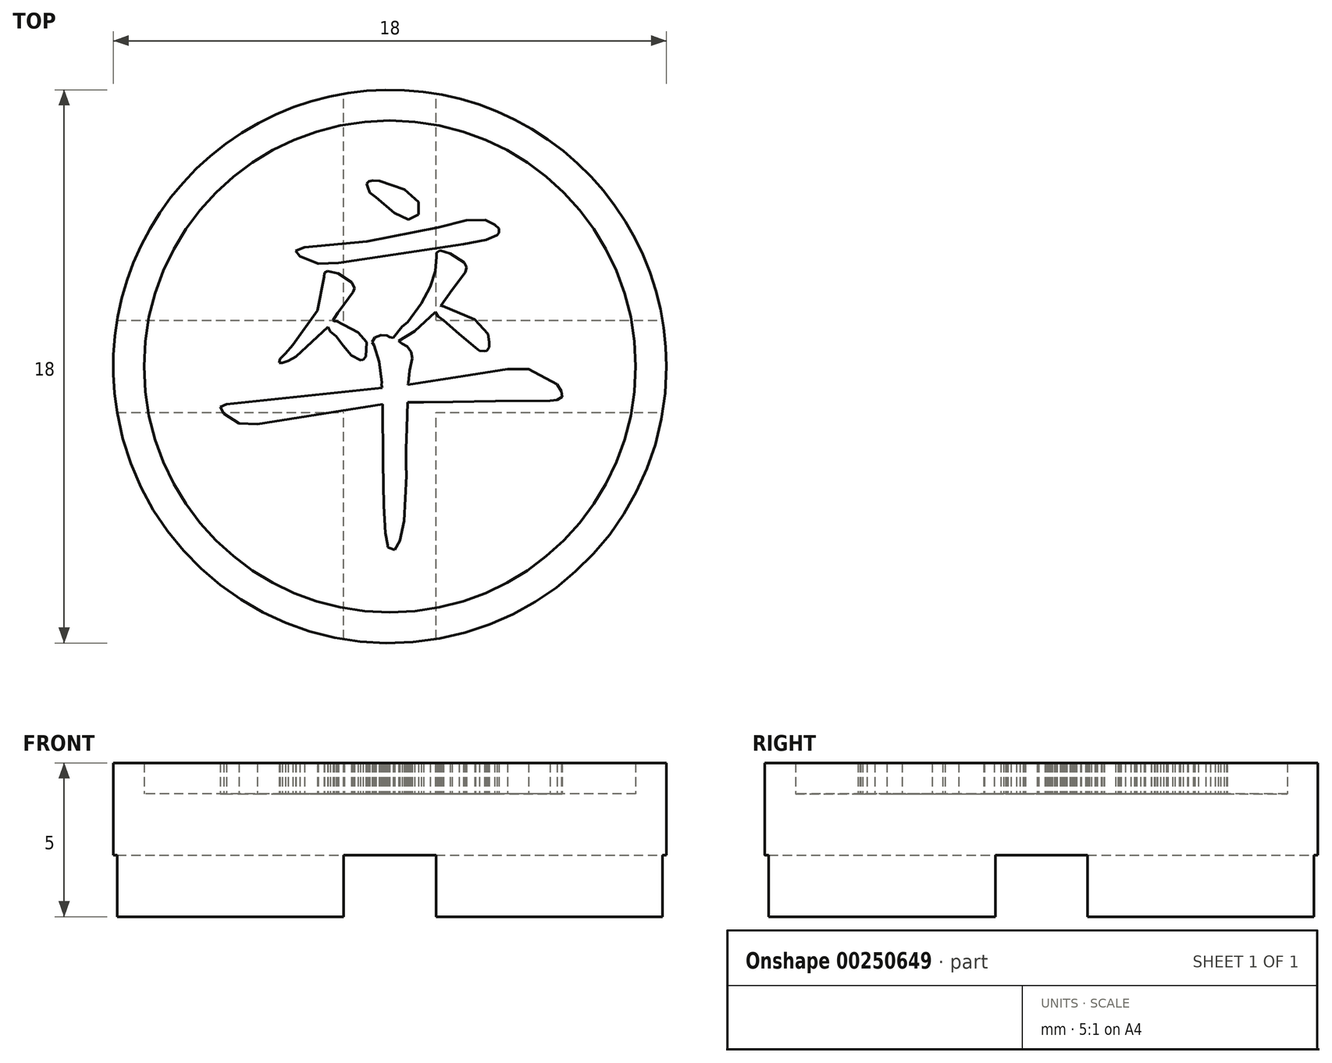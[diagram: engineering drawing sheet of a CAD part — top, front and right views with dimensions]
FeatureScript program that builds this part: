
annotation { "Feature Type Name" : "Feature", "Feature Type Description" : "" }
export const myFeature = defineFeature(function(context is Context, id is Id, definition is map)
    precondition{}
    {
        {
            var Q0;
            Q0=qCreatedBy(makeId("Top.planeOp"),FACE);
            var sketch = newSketch(context, id + "F0", { "sketchPlane" : qUnion([Q0])});
            skCircle(sketch, "E0", {"center": v(-31.33, 19.76) * mm, "radius": 9 * mm});
            skSolve(sketch);
        }
        {
            var Q0;
            Q0=qSketchRegion(id+"F0",true);
            extrude(context, id + "F1", {"entities" : qUnion([Q0]), "depth" : 4 * mm});
        }
        {
            var Q0;
            Q0=makeQuery(id+"F1.opExtrude","CAP_FACE",FACE,{"disambiguationData":[OSD([sQuery(id+"F0.wireOp",EDGE,"E0")])],"isStart":false});
            var sketch = newSketch(context, id + "F2", { "sketchPlane" : qUnion([Q0])});
            skCircle(sketch, "E1", {"center": v(-31.33, 19.76) * mm, "radius": 8 * mm});
            skCircle(sketch, "E2", {"center": v(-31.33, 19.76) * mm, "radius": 9 * mm});
            skSolve(sketch);
        }
        {
            var Q0;
            Q0=makeQuery(id+"F1.opExtrude","CAP_FACE",FACE,{"disambiguationData":[OSD([sQuery(id+"F0.wireOp",EDGE,"E0")])],"isStart":true});
            var sketch = newSketch(context, id + "F3", { "sketchPlane" : qUnion([Q0])});
            skLineSegment(sketch, "E3", {"start": v(-31.33, -19.76) * mm, "end": v(-22.33, -19.76) * mm, "construction": true});
            skLineSegment(sketch, "E4", {"start": v(-31.33, -19.76) * mm, "end": v(-31.33, -10.76) * mm, "construction": true});
            skLineSegment(sketch, "E5", {"start": v(-31.33, -19.76) * mm, "end": v(-40.33, -19.76) * mm, "construction": true});
            skLineSegment(sketch, "E6", {"start": v(-31.33, -19.76) * mm, "end": v(-31.33, -28.76) * mm, "construction": true});
            skLineSegment(sketch, "E7.bottom", {"start": v(-40.33, -28.76) * mm, "end": v(-22.33, -28.76) * mm});
            skLineSegment(sketch, "E7.top", {"start": v(-40.33, -10.76) * mm, "end": v(-22.33, -10.76) * mm});
            skLineSegment(sketch, "E7.left", {"start": v(-22.33, -10.76) * mm, "end": v(-22.33, -28.76) * mm});
            skLineSegment(sketch, "E7.right", {"start": v(-40.33, -10.76) * mm, "end": v(-40.33, -28.76) * mm});
            skPoint(sketch, "E8", {"position": v(-31.33, -28.76) * mm});
            skPoint(sketch, "E9", {"position": v(-40.33, -19.76) * mm});
            skPoint(sketch, "E10", {"position": v(-22.33, -19.76) * mm});
            skPoint(sketch, "E11", {"position": v(-31.33, -10.76) * mm});
            skLineSegment(sketch, "E12.bottom", {"start": v(-32.83, -10.76) * mm, "end": v(-29.83, -10.76) * mm});
            skLineSegment(sketch, "E12.top", {"start": v(-32.83, -28.76) * mm, "end": v(-29.83, -28.76) * mm});
            skLineSegment(sketch, "E12.left", {"start": v(-32.83, -10.76) * mm, "end": v(-32.83, -28.76) * mm});
            skLineSegment(sketch, "E12.right", {"start": v(-29.83, -10.76) * mm, "end": v(-29.83, -28.76) * mm});
            skLineSegment(sketch, "E13.bottom", {"start": v(-40.33, -18.26) * mm, "end": v(-22.33, -18.26) * mm});
            skLineSegment(sketch, "E13.top", {"start": v(-40.33, -21.26) * mm, "end": v(-22.33, -21.26) * mm});
            skLineSegment(sketch, "E13.left", {"start": v(-40.33, -18.26) * mm, "end": v(-40.33, -21.26) * mm});
            skLineSegment(sketch, "E13.right", {"start": v(-22.33, -18.26) * mm, "end": v(-22.33, -21.26) * mm});
            skSolve(sketch);
        }
        {
            var Q0;
            {var subQ1=sQuery(id+"F3.wireOp",EDGE,"E12.bottom");var subQ3=makeQuery(id+"F1.opExtrude","CAP_EDGE",EDGE,{"disambiguationData":[OSD([sQuery(id+"F0.wireOp",EDGE,"E0")])],"isStart":true});var subQ4=makeQuery(id+"F3.imprint","INTERSECT",VERTEX,{"derivedFrom":[subQ3,subQ1]});Q0=makeQuery(id+"F3.imprint","IMPRINT",FACE,{"disambiguationData":[TD([[makeQuery(id+"F3.imprint","IMPRINT",EDGE,{"disambiguationData":[TD([[subQ4,1.0]])],"derivedFrom":subQ3}),1.0]])]});}
            var Q1;
            {var subQ1=sQuery(id+"F3.wireOp",EDGE,"E12.bottom");var subQ3=makeQuery(id+"F1.opExtrude","CAP_EDGE",EDGE,{"disambiguationData":[OSD([sQuery(id+"F0.wireOp",EDGE,"E0")])],"isStart":true});var subQ4=makeQuery(id+"F3.imprint","INTERSECT",VERTEX,{"derivedFrom":[subQ3,subQ1]});Q1=makeQuery(id+"F3.imprint","IMPRINT",FACE,{"disambiguationData":[TD([[makeQuery(id+"F3.imprint","IMPRINT",EDGE,{"disambiguationData":[TD([[subQ4,-1.0]])],"derivedFrom":subQ3}),1.0]])]});}
            var Q2;
            {var subQ1=sQuery(id+"F3.wireOp",EDGE,"E12.top");var subQ3=makeQuery(id+"F1.opExtrude","CAP_EDGE",EDGE,{"disambiguationData":[OSD([sQuery(id+"F0.wireOp",EDGE,"E0")])],"isStart":true});var subQ4=makeQuery(id+"F3.imprint","INTERSECT",VERTEX,{"derivedFrom":[subQ3,subQ1]});Q2=makeQuery(id+"F3.imprint","IMPRINT",FACE,{"disambiguationData":[TD([[makeQuery(id+"F3.imprint","IMPRINT",EDGE,{"disambiguationData":[TD([[subQ4,-1.0]])],"derivedFrom":subQ3}),1.0]])]});}
            var Q3;
            {var subQ1=sQuery(id+"F3.wireOp",EDGE,"E12.top");var subQ3=makeQuery(id+"F1.opExtrude","CAP_EDGE",EDGE,{"disambiguationData":[OSD([sQuery(id+"F0.wireOp",EDGE,"E0")])],"isStart":true});var subQ4=makeQuery(id+"F3.imprint","INTERSECT",VERTEX,{"derivedFrom":[subQ3,subQ1]});Q3=makeQuery(id+"F3.imprint","IMPRINT",FACE,{"disambiguationData":[TD([[makeQuery(id+"F3.imprint","IMPRINT",EDGE,{"disambiguationData":[TD([[subQ4,1.0]])],"derivedFrom":subQ3}),1.0]])]});}
            var Q4;
            {var subQ0=sQuery(id+"F3.wireOp",EDGE,"E13.left");var subQ3=makeQuery(id+"F1.opExtrude","CAP_EDGE",EDGE,{"disambiguationData":[OSD([sQuery(id+"F0.wireOp",EDGE,"E0")])],"isStart":true});var subQ5=makeQuery(id+"F3.imprint","INTERSECT",VERTEX,{"derivedFrom":[subQ3,subQ0]});Q4=makeQuery(id+"F3.imprint","IMPRINT",FACE,{"disambiguationData":[TD([[makeQuery(id+"F3.imprint","IMPRINT",EDGE,{"disambiguationData":[TD([[subQ5,-1.0]])],"derivedFrom":subQ3}),1.0]])]});}
            var Q5;
            {var subQ0=sQuery(id+"F3.wireOp",EDGE,"E13.right");var subQ3=makeQuery(id+"F1.opExtrude","CAP_EDGE",EDGE,{"disambiguationData":[OSD([sQuery(id+"F0.wireOp",EDGE,"E0")])],"isStart":true});var subQ5=makeQuery(id+"F3.imprint","INTERSECT",VERTEX,{"derivedFrom":[subQ3,subQ0]});Q5=makeQuery(id+"F3.imprint","IMPRINT",FACE,{"disambiguationData":[TD([[makeQuery(id+"F3.imprint","IMPRINT",EDGE,{"disambiguationData":[TD([[subQ5,1.0]])],"derivedFrom":subQ3}),1.0]])]});}
            var Q6;
            {var subQ0=sQuery(id+"F3.wireOp",EDGE,"E13.left");var subQ3=makeQuery(id+"F1.opExtrude","CAP_EDGE",EDGE,{"disambiguationData":[OSD([sQuery(id+"F0.wireOp",EDGE,"E0")])],"isStart":true});var subQ5=makeQuery(id+"F3.imprint","INTERSECT",VERTEX,{"derivedFrom":[subQ3,subQ0]});Q6=makeQuery(id+"F3.imprint","IMPRINT",FACE,{"disambiguationData":[TD([[makeQuery(id+"F3.imprint","IMPRINT",EDGE,{"disambiguationData":[TD([[subQ5,1.0]])],"derivedFrom":subQ3}),1.0]])]});}
            var Q7;
            {var subQ0=sQuery(id+"F3.wireOp",EDGE,"E13.right");var subQ3=makeQuery(id+"F1.opExtrude","CAP_EDGE",EDGE,{"disambiguationData":[OSD([sQuery(id+"F0.wireOp",EDGE,"E0")])],"isStart":true});var subQ5=makeQuery(id+"F3.imprint","INTERSECT",VERTEX,{"derivedFrom":[subQ3,subQ0]});Q7=makeQuery(id+"F3.imprint","IMPRINT",FACE,{"disambiguationData":[TD([[makeQuery(id+"F3.imprint","IMPRINT",EDGE,{"disambiguationData":[TD([[subQ5,-1.0]])],"derivedFrom":subQ3}),1.0]])]});}
            var Q8;
            {var subQ3=makeQuery(id+"F1.opExtrude","CAP_EDGE",EDGE,{"disambiguationData":[OSD([sQuery(id+"F0.wireOp",EDGE,"E0")])],"isStart":true});var subQ5=sQuery(id+"F3.wireOp",EDGE,"E12.left");var subQ8=makeQuery(id+"F3.imprint","INTERSECT",VERTEX,{"disambiguationData":[OD(1.0)],"derivedFrom":[subQ3,subQ5]});Q8=makeQuery(id+"F3.imprint","IMPRINT",FACE,{"disambiguationData":[TD([[makeQuery(id+"F3.imprint","IMPRINT",EDGE,{"disambiguationData":[TD([[subQ8,-1.0]])],"derivedFrom":subQ3}),1.0]])]});}
            var Q9;
            {var subQ3=makeQuery(id+"F1.opExtrude","CAP_EDGE",EDGE,{"disambiguationData":[OSD([sQuery(id+"F0.wireOp",EDGE,"E0")])],"isStart":true});var subQ5=sQuery(id+"F3.wireOp",EDGE,"E12.right");var subQ8=makeQuery(id+"F3.imprint","INTERSECT",VERTEX,{"disambiguationData":[OD(1.0)],"derivedFrom":[subQ3,subQ5]});Q9=makeQuery(id+"F3.imprint","IMPRINT",FACE,{"disambiguationData":[TD([[makeQuery(id+"F3.imprint","IMPRINT",EDGE,{"disambiguationData":[TD([[subQ8,1.0]])],"derivedFrom":subQ3}),1.0]])]});}
            var Q10;
            {var subQ3=makeQuery(id+"F1.opExtrude","CAP_EDGE",EDGE,{"disambiguationData":[OSD([sQuery(id+"F0.wireOp",EDGE,"E0")])],"isStart":true});var subQ5=sQuery(id+"F3.wireOp",EDGE,"E12.left");var subQ8=makeQuery(id+"F3.imprint","INTERSECT",VERTEX,{"disambiguationData":[OD(0.0)],"derivedFrom":[subQ3,subQ5]});Q10=makeQuery(id+"F3.imprint","IMPRINT",FACE,{"disambiguationData":[TD([[makeQuery(id+"F3.imprint","IMPRINT",EDGE,{"disambiguationData":[TD([[subQ8,1.0]])],"derivedFrom":subQ3}),1.0]])]});}
            var Q11;
            {var subQ3=makeQuery(id+"F1.opExtrude","CAP_EDGE",EDGE,{"disambiguationData":[OSD([sQuery(id+"F0.wireOp",EDGE,"E0")])],"isStart":true});var subQ5=sQuery(id+"F3.wireOp",EDGE,"E12.right");var subQ8=makeQuery(id+"F3.imprint","INTERSECT",VERTEX,{"disambiguationData":[OD(0.0)],"derivedFrom":[subQ3,subQ5]});Q11=makeQuery(id+"F3.imprint","IMPRINT",FACE,{"disambiguationData":[TD([[makeQuery(id+"F3.imprint","IMPRINT",EDGE,{"disambiguationData":[TD([[subQ8,-1.0]])],"derivedFrom":subQ3}),1.0]])]});}
            var Q12;
            {var subQ2=sQuery(id+"F3.wireOp",EDGE,"E12.left");var subQ4=sQuery(id+"F3.wireOp",EDGE,"E13.bottom");var subQ8=makeQuery(id+"F3.imprint","INTERSECT",VERTEX,{"derivedFrom":[subQ2,subQ4]});Q12=makeQuery(id+"F3.imprint","IMPRINT",FACE,{"disambiguationData":[TD([[makeQuery(id+"F3.imprint","IMPRINT",EDGE,{"disambiguationData":[TD([[subQ8,1.0]])],"derivedFrom":subQ2}),1.0]])]});}
            var Q13;
            {var subQ1=sQuery(id+"F3.wireOp",EDGE,"E12.left");var subQ5=sQuery(id+"F3.wireOp",EDGE,"E13.bottom");var subQ6=makeQuery(id+"F3.imprint","INTERSECT",VERTEX,{"derivedFrom":[subQ1,subQ5]});Q13=makeQuery(id+"F3.imprint","IMPRINT",FACE,{"disambiguationData":[TD([[makeQuery(id+"F3.imprint","IMPRINT",EDGE,{"disambiguationData":[TD([[subQ6,-1.0]])],"derivedFrom":subQ1}),-1.0]])]});}
            var Q14;
            {var subQ0=sQuery(id+"F3.wireOp",EDGE,"E13.top");var subQ1=sQuery(id+"F3.wireOp",EDGE,"E12.left");var subQ2=makeQuery(id+"F3.imprint","INTERSECT",VERTEX,{"derivedFrom":[subQ1,subQ0]});Q14=makeQuery(id+"F3.imprint","IMPRINT",FACE,{"disambiguationData":[TD([[makeQuery(id+"F3.imprint","IMPRINT",EDGE,{"disambiguationData":[TD([[subQ2,-1.0]])],"derivedFrom":subQ1}),1.0]])]});}
            var Q15;
            {var subQ2=sQuery(id+"F3.wireOp",EDGE,"E13.bottom");var subQ5=sQuery(id+"F3.wireOp",EDGE,"E12.right");var subQ8=makeQuery(id+"F3.imprint","INTERSECT",VERTEX,{"derivedFrom":[subQ5,subQ2]});Q15=makeQuery(id+"F3.imprint","IMPRINT",FACE,{"disambiguationData":[TD([[makeQuery(id+"F3.imprint","IMPRINT",EDGE,{"disambiguationData":[TD([[subQ8,-1.0]])],"derivedFrom":subQ5}),1.0]])]});}
            var Q16;
            {var subQ0=sQuery(id+"F3.wireOp",EDGE,"E13.bottom");var subQ1=sQuery(id+"F3.wireOp",EDGE,"E12.left");var subQ2=makeQuery(id+"F3.imprint","INTERSECT",VERTEX,{"derivedFrom":[subQ1,subQ0]});Q16=makeQuery(id+"F3.imprint","IMPRINT",FACE,{"disambiguationData":[TD([[makeQuery(id+"F3.imprint","IMPRINT",EDGE,{"disambiguationData":[TD([[subQ2,-1.0]])],"derivedFrom":subQ1}),1.0]])]});}
            extrude(context, id + "F4", {"entities" : qUnion([Q0, Q1, Q2, Q3, Q4, Q5, Q6, Q7, Q8, Q9, Q10, Q11, Q12, Q13, Q14, Q15, Q16]), "operationType" : NewBodyOperationType.REMOVE, "oppositeDirection" : true, "depth" : 2 * mm});
        }
        {
            var Q0;
            Q0=qSketchRegion(id+"F2",true);
            var Q1;
            Q1=makeQuery(id+"F2.imprint","IMPRINT",FACE,{"disambiguationData":[TD([[makeQuery(id+"F2.imprint","IMPRINT",EDGE,{"derivedFrom":sQuery(id+"F2.wireOp",EDGE,"hKqnuJLd-dfdz-vJIs-yDKo-c4hLNRw30SuP")}),-1.0]])]});
            extrude(context, id + "F5", {"entities" : qUnion([Q0, Q1]), "operationType" : NewBodyOperationType.ADD, "depth" : 1 * mm});
        }
        {
            var Q0;
            Q0=makeQuery(id+"F1.opExtrude","CAP_FACE",FACE,{"disambiguationData":[OSD([sQuery(id+"F0.wireOp",EDGE,"E0")])],"isStart":false});
            var sketch = newSketch(context, id + "F6", { "sketchPlane" : qUnion([Q0])});
            skLineSegment(sketch, "E14", {"start": v(-31.78, 25.26) * mm, "end": v(-31.19, 24.76) * mm});
            skLineSegment(sketch, "E15", {"start": v(-31.19, 24.76) * mm, "end": v(-30.72, 24.53) * mm});
            skLineSegment(sketch, "E16", {"start": v(-30.72, 24.53) * mm, "end": v(-30.4, 24.7) * mm});
            skLineSegment(sketch, "E17", {"start": v(-30.4, 24.7) * mm, "end": v(-30.4, 24.87) * mm});
            skLineSegment(sketch, "E18", {"start": v(-30.4, 24.87) * mm, "end": v(-30.4, 25.1) * mm});
            skLineSegment(sketch, "E19", {"start": v(-30.4, 25.1) * mm, "end": v(-30.85, 25.52) * mm});
            skLineSegment(sketch, "E20", {"start": v(-30.85, 25.52) * mm, "end": v(-31.66, 25.8) * mm});
            skLineSegment(sketch, "E21", {"start": v(-31.66, 25.8) * mm, "end": v(-31.88, 25.8) * mm});
            skLineSegment(sketch, "E22", {"start": v(-31.88, 25.8) * mm, "end": v(-32, 25.78) * mm});
            skLineSegment(sketch, "E23", {"start": v(-32, 25.78) * mm, "end": v(-32.09, 25.7) * mm});
            skLineSegment(sketch, "E24", {"start": v(-32.09, 25.7) * mm, "end": v(-32.04, 25.59) * mm});
            skLineSegment(sketch, "E25", {"start": v(-32.04, 25.59) * mm, "end": v(-31.98, 25.42) * mm});
            skLineSegment(sketch, "E26", {"start": v(-31.98, 25.42) * mm, "end": v(-31.78, 25.26) * mm});
            skLineSegment(sketch, "E27", {"start": v(-34.1, 23.64) * mm, "end": v(-34.4, 23.52) * mm});
            skLineSegment(sketch, "E28", {"start": v(-34.4, 23.52) * mm, "end": v(-34.25, 23.35) * mm});
            skLineSegment(sketch, "E29", {"start": v(-34.25, 23.35) * mm, "end": v(-33.66, 23.1) * mm});
            skLineSegment(sketch, "E30", {"start": v(-33.66, 23.1) * mm, "end": v(-33, 23.13) * mm});
            skLineSegment(sketch, "E31", {"start": v(-33, 23.13) * mm, "end": v(-28.93, 23.73) * mm});
            skLineSegment(sketch, "E32", {"start": v(-28.93, 23.73) * mm, "end": v(-28.2, 23.88) * mm});
            skLineSegment(sketch, "E33", {"start": v(-28.2, 23.88) * mm, "end": v(-27.84, 24.03) * mm});
            skLineSegment(sketch, "E34", {"start": v(-27.84, 24.03) * mm, "end": v(-27.78, 24.1) * mm});
            skLineSegment(sketch, "E35", {"start": v(-27.78, 24.1) * mm, "end": v(-27.77, 24.24) * mm});
            skLineSegment(sketch, "E36", {"start": v(-27.77, 24.24) * mm, "end": v(-27.93, 24.37) * mm});
            skLineSegment(sketch, "E37", {"start": v(-27.93, 24.37) * mm, "end": v(-28.22, 24.52) * mm});
            skLineSegment(sketch, "E38", {"start": v(-28.22, 24.52) * mm, "end": v(-28.84, 24.51) * mm});
            skLineSegment(sketch, "E39", {"start": v(-28.84, 24.51) * mm, "end": v(-29.75, 24.28) * mm});
            skLineSegment(sketch, "E40", {"start": v(-29.75, 24.28) * mm, "end": v(-32.07, 23.82) * mm});
            skLineSegment(sketch, "E41", {"start": v(-32.07, 23.82) * mm, "end": v(-34.1, 23.64) * mm});
            skLineSegment(sketch, "E42", {"start": v(-33.34, 21.04) * mm, "end": v(-33.26, 20.9) * mm});
            skLineSegment(sketch, "E43", {"start": v(-33.26, 20.9) * mm, "end": v(-33.07, 20.73) * mm});
            skLineSegment(sketch, "E44", {"start": v(-33.07, 20.73) * mm, "end": v(-32.85, 20.44) * mm});
            skLineSegment(sketch, "E45", {"start": v(-32.85, 20.44) * mm, "end": v(-32.58, 20.12) * mm});
            skLineSegment(sketch, "E46", {"start": v(-32.58, 20.12) * mm, "end": v(-32.29, 19.96) * mm});
            skLineSegment(sketch, "E47", {"start": v(-32.29, 19.96) * mm, "end": v(-32.2, 19.98) * mm});
            skLineSegment(sketch, "E48", {"start": v(-32.2, 19.98) * mm, "end": v(-32.1, 20.08) * mm});
            skLineSegment(sketch, "E49", {"start": v(-32.1, 20.08) * mm, "end": v(-32.08, 20.54) * mm});
            skLineSegment(sketch, "E50", {"start": v(-32.08, 20.54) * mm, "end": v(-32.37, 20.87) * mm});
            skLineSegment(sketch, "E51", {"start": v(-32.37, 20.87) * mm, "end": v(-33.06, 21.23) * mm});
            skLineSegment(sketch, "E52", {"start": v(-33.06, 21.23) * mm, "end": v(-33.15, 21.23) * mm});
            skLineSegment(sketch, "E53", {"start": v(-33.15, 21.23) * mm, "end": v(-33.18, 21.26) * mm});
            skLineSegment(sketch, "E54", {"start": v(-33.18, 21.26) * mm, "end": v(-33.15, 21.32) * mm});
            skLineSegment(sketch, "E55", {"start": v(-33.15, 21.32) * mm, "end": v(-33.02, 21.5) * mm});
            skLineSegment(sketch, "E56", {"start": v(-33.02, 21.5) * mm, "end": v(-32.81, 21.8) * mm});
            skLineSegment(sketch, "E57", {"start": v(-32.81, 21.8) * mm, "end": v(-32.53, 22.17) * mm});
            skLineSegment(sketch, "E58", {"start": v(-32.53, 22.17) * mm, "end": v(-32.49, 22.3) * mm});
            skLineSegment(sketch, "E59", {"start": v(-32.49, 22.3) * mm, "end": v(-32.56, 22.49) * mm});
            skLineSegment(sketch, "E60", {"start": v(-32.56, 22.49) * mm, "end": v(-33.02, 22.78) * mm});
            skLineSegment(sketch, "E61", {"start": v(-33.02, 22.78) * mm, "end": v(-33.35, 22.87) * mm});
            skLineSegment(sketch, "E62", {"start": v(-33.35, 22.87) * mm, "end": v(-33.46, 22.8) * mm});
            skLineSegment(sketch, "E63", {"start": v(-33.46, 22.8) * mm, "end": v(-33.47, 22.68) * mm});
            skLineSegment(sketch, "E64", {"start": v(-33.47, 22.68) * mm, "end": v(-33.69, 21.58) * mm});
            skLineSegment(sketch, "E65", {"start": v(-33.69, 21.58) * mm, "end": v(-34.48, 20.46) * mm});
            skLineSegment(sketch, "E66", {"start": v(-34.48, 20.46) * mm, "end": v(-34.73, 20.18) * mm});
            skLineSegment(sketch, "E67", {"start": v(-34.73, 20.18) * mm, "end": v(-34.9, 20) * mm});
            skLineSegment(sketch, "E68", {"start": v(-34.9, 20) * mm, "end": v(-34.93, 19.88) * mm});
            skLineSegment(sketch, "E69", {"start": v(-34.93, 19.88) * mm, "end": v(-34.83, 19.88) * mm});
            skLineSegment(sketch, "E70", {"start": v(-34.83, 19.88) * mm, "end": v(-34.64, 19.94) * mm});
            skLineSegment(sketch, "E71", {"start": v(-34.64, 19.94) * mm, "end": v(-34.38, 20.08) * mm});
            skLineSegment(sketch, "E72", {"start": v(-34.38, 20.08) * mm, "end": v(-33.34, 21.04) * mm});
            skLineSegment(sketch, "E73", {"start": v(-31.56, 18.54) * mm, "end": v(-31.55, 16.62) * mm});
            skLineSegment(sketch, "E74", {"start": v(-31.55, 16.62) * mm, "end": v(-31.52, 15.23) * mm});
            skLineSegment(sketch, "E75", {"start": v(-31.52, 15.23) * mm, "end": v(-31.47, 14.34) * mm});
            skLineSegment(sketch, "E76", {"start": v(-31.47, 14.34) * mm, "end": v(-31.4, 13.94) * mm});
            skLineSegment(sketch, "E77", {"start": v(-31.4, 13.94) * mm, "end": v(-31.4, 13.88) * mm});
            skLineSegment(sketch, "E78", {"start": v(-31.4, 13.88) * mm, "end": v(-31.34, 13.86) * mm});
            skLineSegment(sketch, "E79", {"start": v(-31.34, 13.86) * mm, "end": v(-31.17, 13.8) * mm});
            skLineSegment(sketch, "E80", {"start": v(-31.17, 13.8) * mm, "end": v(-31, 14.08) * mm});
            skLineSegment(sketch, "E81", {"start": v(-31, 14.08) * mm, "end": v(-30.86, 14.73) * mm});
            skLineSegment(sketch, "E82", {"start": v(-30.86, 14.73) * mm, "end": v(-30.79, 16.2) * mm});
            skLineSegment(sketch, "E83", {"start": v(-30.79, 16.2) * mm, "end": v(-30.8, 16.55) * mm});
            skLineSegment(sketch, "E84", {"start": v(-30.8, 16.55) * mm, "end": v(-30.8, 17.06) * mm});
            skLineSegment(sketch, "E85", {"start": v(-30.8, 17.06) * mm, "end": v(-30.78, 17.75) * mm});
            skLineSegment(sketch, "E86", {"start": v(-30.78, 17.75) * mm, "end": v(-30.75, 18.6) * mm});
            skLineSegment(sketch, "E87", {"start": v(-30.75, 18.6) * mm, "end": v(-30.23, 18.59) * mm});
            skLineSegment(sketch, "E88", {"start": v(-30.23, 18.59) * mm, "end": v(-29.27, 18.6) * mm});
            skLineSegment(sketch, "E89", {"start": v(-29.27, 18.6) * mm, "end": v(-27.9, 18.63) * mm});
            skLineSegment(sketch, "E90", {"start": v(-27.9, 18.63) * mm, "end": v(-26.12, 18.65) * mm});
            skLineSegment(sketch, "E91", {"start": v(-26.12, 18.65) * mm, "end": v(-25.89, 18.67) * mm});
            skLineSegment(sketch, "E92", {"start": v(-25.89, 18.67) * mm, "end": v(-25.73, 18.77) * mm});
            skLineSegment(sketch, "E93", {"start": v(-25.73, 18.77) * mm, "end": v(-25.75, 18.95) * mm});
            skLineSegment(sketch, "E94", {"start": v(-25.75, 18.95) * mm, "end": v(-25.9, 19.18) * mm});
            skLineSegment(sketch, "E95", {"start": v(-25.9, 19.18) * mm, "end": v(-26.81, 19.67) * mm});
            skLineSegment(sketch, "E96", {"start": v(-26.81, 19.67) * mm, "end": v(-27.5, 19.67) * mm});
            skLineSegment(sketch, "E97", {"start": v(-27.5, 19.67) * mm, "end": v(-28.95, 19.44) * mm});
            skLineSegment(sketch, "E98", {"start": v(-28.95, 19.44) * mm, "end": v(-30.73, 19.17) * mm});
            skLineSegment(sketch, "E99", {"start": v(-30.73, 19.17) * mm, "end": v(-30.76, 19.19) * mm});
            skLineSegment(sketch, "E100", {"start": v(-30.76, 19.19) * mm, "end": v(-30.72, 19.23) * mm});
            skLineSegment(sketch, "E101", {"start": v(-30.72, 19.23) * mm, "end": v(-30.69, 19.62) * mm});
            skLineSegment(sketch, "E102", {"start": v(-30.69, 19.62) * mm, "end": v(-30.6, 20.04) * mm});
            skLineSegment(sketch, "E103", {"start": v(-30.6, 20.04) * mm, "end": v(-30.64, 20.23) * mm});
            skLineSegment(sketch, "E104", {"start": v(-30.64, 20.23) * mm, "end": v(-30.76, 20.42) * mm});
            skLineSegment(sketch, "E105", {"start": v(-30.76, 20.42) * mm, "end": v(-30.93, 20.5) * mm});
            skLineSegment(sketch, "E106", {"start": v(-30.93, 20.5) * mm, "end": v(-31.04, 20.6) * mm});
            skLineSegment(sketch, "E107", {"start": v(-31.04, 20.6) * mm, "end": v(-30.52, 20.91) * mm});
            skLineSegment(sketch, "E108", {"start": v(-30.52, 20.91) * mm, "end": v(-29.85, 21.52) * mm});
            skLineSegment(sketch, "E109", {"start": v(-29.85, 21.52) * mm, "end": v(-29.76, 21.39) * mm});
            skLineSegment(sketch, "E110", {"start": v(-29.76, 21.39) * mm, "end": v(-29.58, 21.26) * mm});
            skLineSegment(sketch, "E111", {"start": v(-29.58, 21.26) * mm, "end": v(-29.08, 20.82) * mm});
            skLineSegment(sketch, "E112", {"start": v(-29.08, 20.82) * mm, "end": v(-28.54, 20.37) * mm});
            skLineSegment(sketch, "E113", {"start": v(-28.54, 20.37) * mm, "end": v(-28.41, 20.26) * mm});
            skLineSegment(sketch, "E114", {"start": v(-28.41, 20.26) * mm, "end": v(-28.25, 20.25) * mm});
            skLineSegment(sketch, "E115", {"start": v(-28.25, 20.25) * mm, "end": v(-28.17, 20.27) * mm});
            skLineSegment(sketch, "E116", {"start": v(-28.17, 20.27) * mm, "end": v(-28.1, 20.39) * mm});
            skLineSegment(sketch, "E117", {"start": v(-28.1, 20.39) * mm, "end": v(-28.1, 20.55) * mm});
            skLineSegment(sketch, "E118", {"start": v(-28.1, 20.55) * mm, "end": v(-28.13, 20.82) * mm});
            skLineSegment(sketch, "E119", {"start": v(-28.13, 20.82) * mm, "end": v(-28.57, 21.28) * mm});
            skLineSegment(sketch, "E120", {"start": v(-28.57, 21.28) * mm, "end": v(-29.62, 21.72) * mm});
            skLineSegment(sketch, "E121", {"start": v(-29.62, 21.72) * mm, "end": v(-29.66, 21.71) * mm});
            skLineSegment(sketch, "E122", {"start": v(-29.66, 21.71) * mm, "end": v(-29.67, 21.72) * mm});
            skLineSegment(sketch, "E123", {"start": v(-29.67, 21.72) * mm, "end": v(-29.3, 22.25) * mm});
            skLineSegment(sketch, "E124", {"start": v(-29.3, 22.25) * mm, "end": v(-28.87, 22.83) * mm});
            skLineSegment(sketch, "E125", {"start": v(-28.87, 22.83) * mm, "end": v(-28.84, 22.98) * mm});
            skLineSegment(sketch, "E126", {"start": v(-28.84, 22.98) * mm, "end": v(-28.9, 23.15) * mm});
            skLineSegment(sketch, "E127", {"start": v(-28.9, 23.15) * mm, "end": v(-29.37, 23.44) * mm});
            skLineSegment(sketch, "E128", {"start": v(-29.37, 23.44) * mm, "end": v(-29.7, 23.53) * mm});
            skLineSegment(sketch, "E129", {"start": v(-29.7, 23.53) * mm, "end": v(-29.81, 23.46) * mm});
            skLineSegment(sketch, "E130", {"start": v(-29.81, 23.46) * mm, "end": v(-29.8, 23.33) * mm});
            skLineSegment(sketch, "E131", {"start": v(-29.8, 23.33) * mm, "end": v(-29.85, 22.86) * mm});
            skLineSegment(sketch, "E132", {"start": v(-29.85, 22.86) * mm, "end": v(-30, 22.36) * mm});
            skLineSegment(sketch, "E133", {"start": v(-30, 22.36) * mm, "end": v(-30.3, 21.8) * mm});
            skLineSegment(sketch, "E134", {"start": v(-30.3, 21.8) * mm, "end": v(-30.75, 21.2) * mm});
            skLineSegment(sketch, "E135", {"start": v(-30.75, 21.2) * mm, "end": v(-30.93, 21.06) * mm});
            skLineSegment(sketch, "E136", {"start": v(-30.93, 21.06) * mm, "end": v(-31.22, 20.68) * mm});
            skLineSegment(sketch, "E137", {"start": v(-31.22, 20.68) * mm, "end": v(-31.34, 20.72) * mm});
            skLineSegment(sketch, "E138", {"start": v(-31.34, 20.72) * mm, "end": v(-31.42, 20.76) * mm});
            skLineSegment(sketch, "E139", {"start": v(-31.42, 20.76) * mm, "end": v(-31.62, 20.78) * mm});
            skLineSegment(sketch, "E140", {"start": v(-31.62, 20.78) * mm, "end": v(-31.81, 20.7) * mm});
            skLineSegment(sketch, "E141", {"start": v(-31.81, 20.7) * mm, "end": v(-31.9, 20.55) * mm});
            skLineSegment(sketch, "E142", {"start": v(-31.9, 20.55) * mm, "end": v(-31.84, 20.44) * mm});
            skLineSegment(sketch, "E143", {"start": v(-31.84, 20.44) * mm, "end": v(-31.68, 19.92) * mm});
            skLineSegment(sketch, "E144", {"start": v(-31.68, 19.92) * mm, "end": v(-31.59, 19.25) * mm});
            skLineSegment(sketch, "E145", {"start": v(-31.59, 19.25) * mm, "end": v(-31.6, 19.16) * mm});
            skLineSegment(sketch, "E146", {"start": v(-31.6, 19.16) * mm, "end": v(-31.57, 19.07) * mm});
            skLineSegment(sketch, "E147", {"start": v(-31.57, 19.07) * mm, "end": v(-36.65, 18.54) * mm});
            skLineSegment(sketch, "E148", {"start": v(-36.65, 18.54) * mm, "end": v(-36.85, 18.44) * mm});
            skLineSegment(sketch, "E149", {"start": v(-36.85, 18.44) * mm, "end": v(-36.74, 18.23) * mm});
            skLineSegment(sketch, "E150", {"start": v(-36.74, 18.23) * mm, "end": v(-36.24, 17.9) * mm});
            skLineSegment(sketch, "E151", {"start": v(-36.24, 17.9) * mm, "end": v(-35.64, 17.89) * mm});
            skLineSegment(sketch, "E152", {"start": v(-35.64, 17.89) * mm, "end": v(-31.56, 18.54) * mm});
            skSolve(sketch);
        }
        {
            var Q0;
            Q0 = qSketchRegion(id + "F6", true);
            extrude(context, id + "F7", {"entities" : qUnion([Q0]), "operationType" : NewBodyOperationType.ADD, "depth" : 1 * mm});
        }
    });
